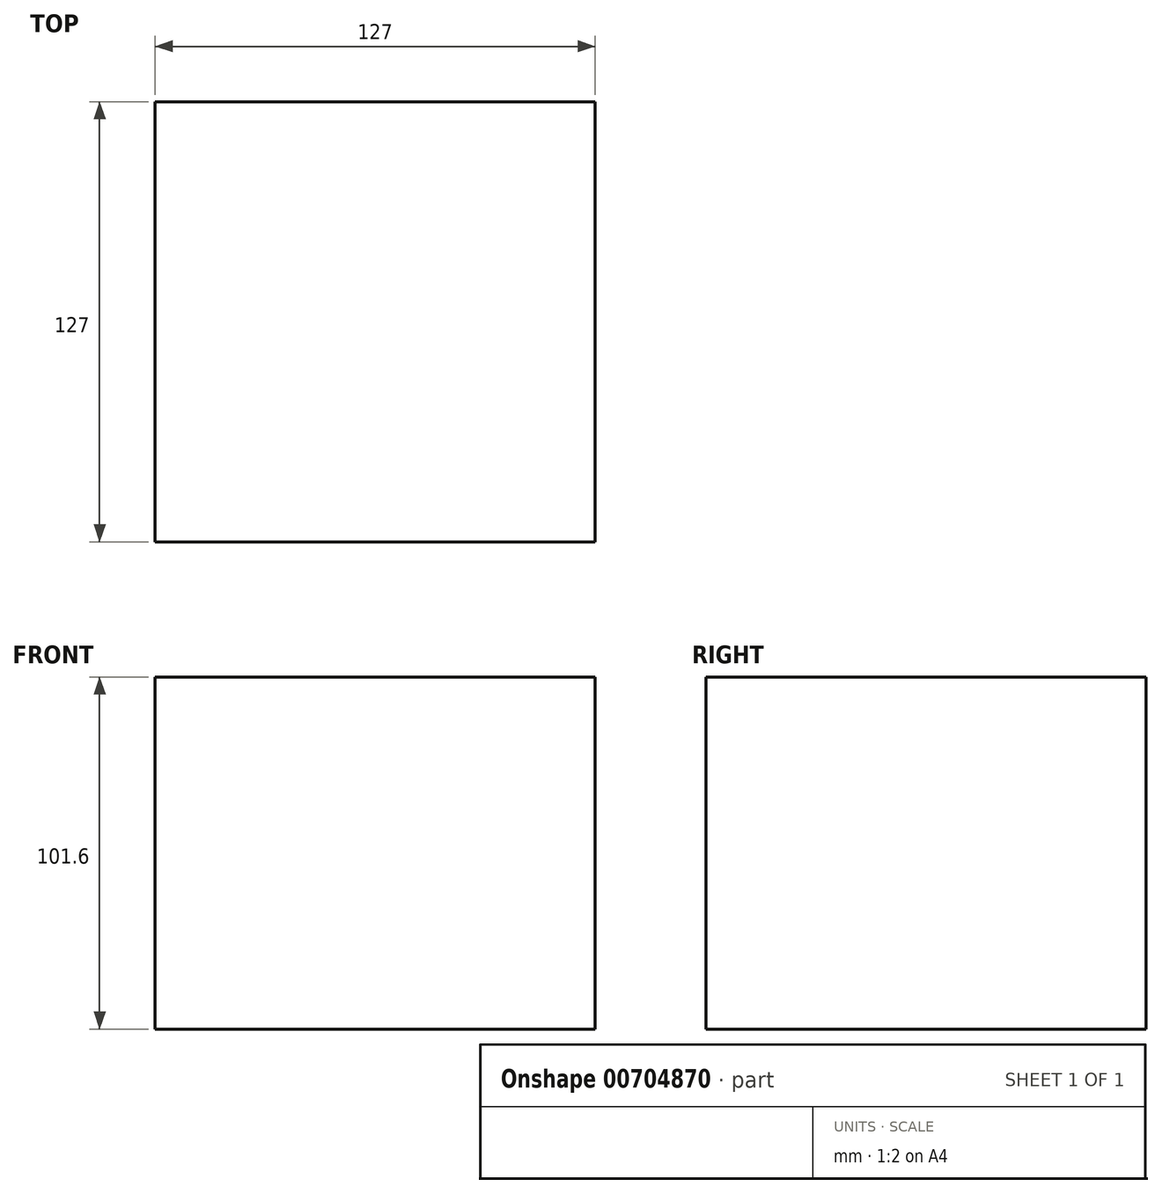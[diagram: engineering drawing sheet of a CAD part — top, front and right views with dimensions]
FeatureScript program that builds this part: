
annotation { "Feature Type Name" : "Feature", "Feature Type Description" : "" }
export const myFeature = defineFeature(function(context is Context, id is Id, definition is map)
    precondition{}
    {
        {
            var Q0;
            Q0=qCreatedBy(makeId("Top.planeOp"),FACE);
            var sketch = newSketch(context, id + "F0", { "sketchPlane" : qUnion([Q0])});
            skLineSegment(sketch, "E0.bottom", {"start": v(61.12, 47.6) * mm, "end": v(-65.88, 47.6) * mm});
            skLineSegment(sketch, "E0.top", {"start": v(61.12, -79.4) * mm, "end": v(-65.88, -79.4) * mm});
            skLineSegment(sketch, "E0.left", {"start": v(61.12, 47.6) * mm, "end": v(61.12, -79.4) * mm});
            skLineSegment(sketch, "E0.right", {"start": v(-65.88, 47.6) * mm, "end": v(-65.88, -79.4) * mm});
            skSolve(sketch);
        }
        {
            var Q0;
            Q0=makeQuery(id+"F0.imprint","IMPRINT",FACE,{"disambiguationData":[TD([[makeQuery(id+"F0.imprint","IMPRINT",EDGE,{"derivedFrom":sQuery(id+"F0.wireOp",EDGE,"E0.bottom")}),1.0]])]});
            extrude(context, id + "F1", {"entities" : qUnion([Q0]), "depth" : 101.6 * mm, "offsetDistance" : 25.4 * mm});
        }
    });
